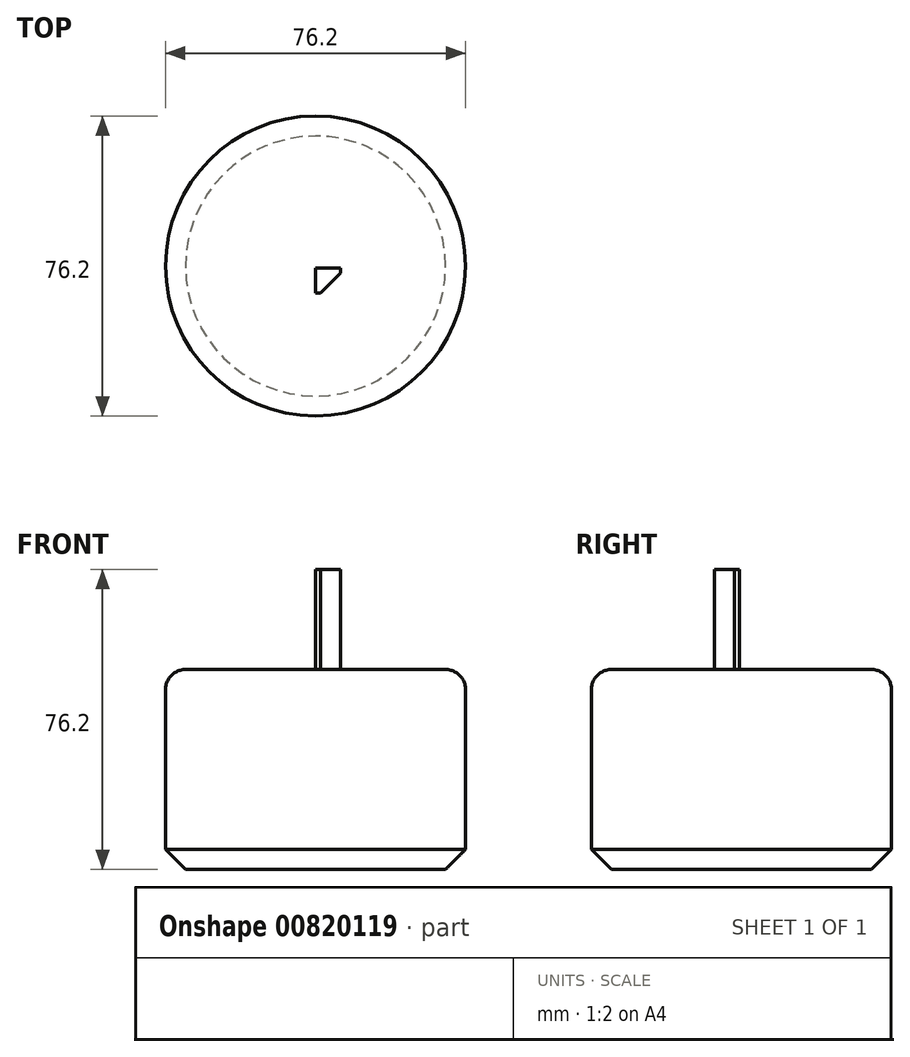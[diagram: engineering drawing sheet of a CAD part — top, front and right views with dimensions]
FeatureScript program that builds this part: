
annotation { "Feature Type Name" : "Feature", "Feature Type Description" : "" }
export const myFeature = defineFeature(function(context is Context, id is Id, definition is map)
    precondition{}
    {
        {
            var Q0;
            Q0=qCreatedBy(makeId("Top.planeOp"),FACE);
            var sketch = newSketch(context, id + "F0", { "sketchPlane" : qUnion([Q0])});
            skCircle(sketch, "E0", {"center": v(0, 0) * mm, "radius": 38.1 * mm});
            skSolve(sketch);
        }
        {
            var Q0;
            Q0 = qSketchRegion(id + "F0", true);
            extrude(context, id + "F1", {"entities" : qUnion([Q0]), "depth" : 50.8 * mm, "offsetDistance" : 25.4 * mm});
        }
        {
            var Q0;
            Q0=qCreatedBy(makeId("Top.planeOp"),FACE);
            var sketch = newSketch(context, id + "F2", { "sketchPlane" : qUnion([Q0])});
            skLineSegment(sketch, "E1.bottom", {"start": v(0, -0.55) * mm, "end": v(6.35, -0.55) * mm});
            skLineSegment(sketch, "E1.top", {"start": v(0, -6.9) * mm, "end": v(6.35, -6.9) * mm});
            skLineSegment(sketch, "E1.left", {"start": v(0, -0.55) * mm, "end": v(0, -6.9) * mm});
            skLineSegment(sketch, "E1.right", {"start": v(6.35, -0.55) * mm, "end": v(6.35, -6.9) * mm});
            skSolve(sketch);
        }
        {
            var Q0;
            Q0 = qSketchRegion(id + "F2", true);
            extrude(context, id + "F3", {"entities" : qUnion([Q0]), "operationType" : NewBodyOperationType.ADD, "depth" : 76.2 * mm, "offsetDistance" : 25.4 * mm});
        }
        {
            var Q0;
            Q0=makeQuery(id+"F1.opExtrude","CAP_EDGE",EDGE,{"disambiguationData":[OSD([sQuery(id+"F0.wireOp",EDGE,"E0")])],"isStart":false});
            fillet(context, id + "F4", {"entities" : qUnion([Q0]), "radius" : 5.08 * mm, "tangentPropagation" : true, "allowEdgeOverflow" : false});
        }
        {
            var Q0;
            Q0=makeQuery(id+"F3.opExtrude","SWEPT_EDGE",EDGE,{"disambiguationData":[OSD([sQuery(id+"F2.wireOp",EDGE,"E1.top"),sQuery(id+"F2.wireOp",EDGE,"E1.right")])]});
            var Q1;
            Q1=makeQuery(id+"F1.opExtrude","CAP_EDGE",EDGE,{"disambiguationData":[OSD([sQuery(id+"F0.wireOp",EDGE,"E0")])],"isStart":true});
            chamfer(context, id + "F5", {"entities" : qUnion([Q0, Q1]), "width" : 5.08 * mm, "tangentPropagation" : true});
        }
    });
